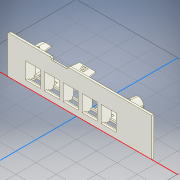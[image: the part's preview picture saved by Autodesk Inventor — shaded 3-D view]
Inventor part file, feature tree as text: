
AUTODESK INVENTOR PART (.ipt)
format: ipt  version: 2022 (Build 260153000, 153)  size: 378,880 bytes
history: native  units: mm
features: other x2, extrude x1, sketch x1
ambient origin geometry x8: Origin, YZ Plane, XZ Plane, XY Plane, X Axis, Y Axis, Z Axis, Center Point
bodies: Body1 (feature_tree)
feature tree (4):
  other  "Твердое тело1"
  extrude  "Выдавливание1"  Depth=17.135mm
  sketch  "Эскиз1"
  other  "Cover Plate_1:1"
